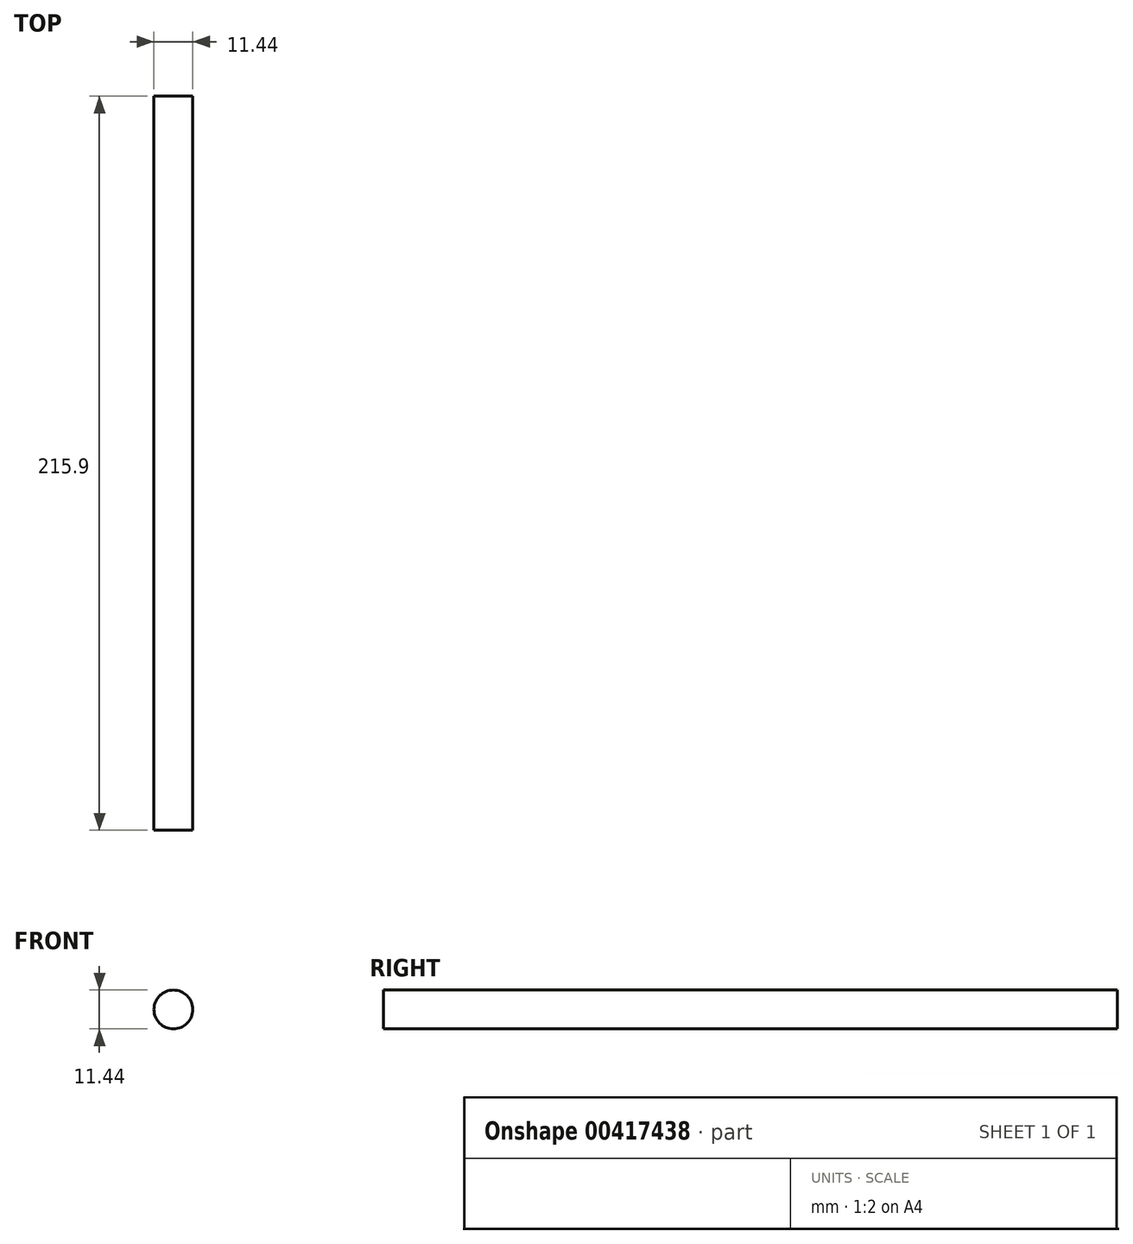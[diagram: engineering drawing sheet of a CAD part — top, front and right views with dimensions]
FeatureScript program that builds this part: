
annotation { "Feature Type Name" : "Feature", "Feature Type Description" : "" }
export const myFeature = defineFeature(function(context is Context, id is Id, definition is map)
    precondition{}
    {
        {
            var Q0;
            Q0=qCreatedBy(makeId("Front.planeOp"),FACE);
            var sketch = newSketch(context, id + "F0", { "sketchPlane" : qUnion([Q0])});
            skCircle(sketch, "E0", {"center": v(0, 0) * mm, "radius": 5.72 * mm});
            skSolve(sketch);
        }
        {
            var Q0;
            Q0=makeQuery(id+"F0.imprint","IMPRINT",FACE,{"disambiguationData":[TD([[makeQuery(id+"F0.imprint","IMPRINT",EDGE,{"derivedFrom":sQuery(id+"F0.wireOp",EDGE,"E0")}),1.0]])]});
            extrude(context, id + "F1", {"entities" : qUnion([Q0]), "depth" : 107.95 * mm, "hasSecondDirection" : true, "secondDirectionOppositeDirection" : true, "secondDirectionDepth" : 107.95 * mm});
        }
    });
